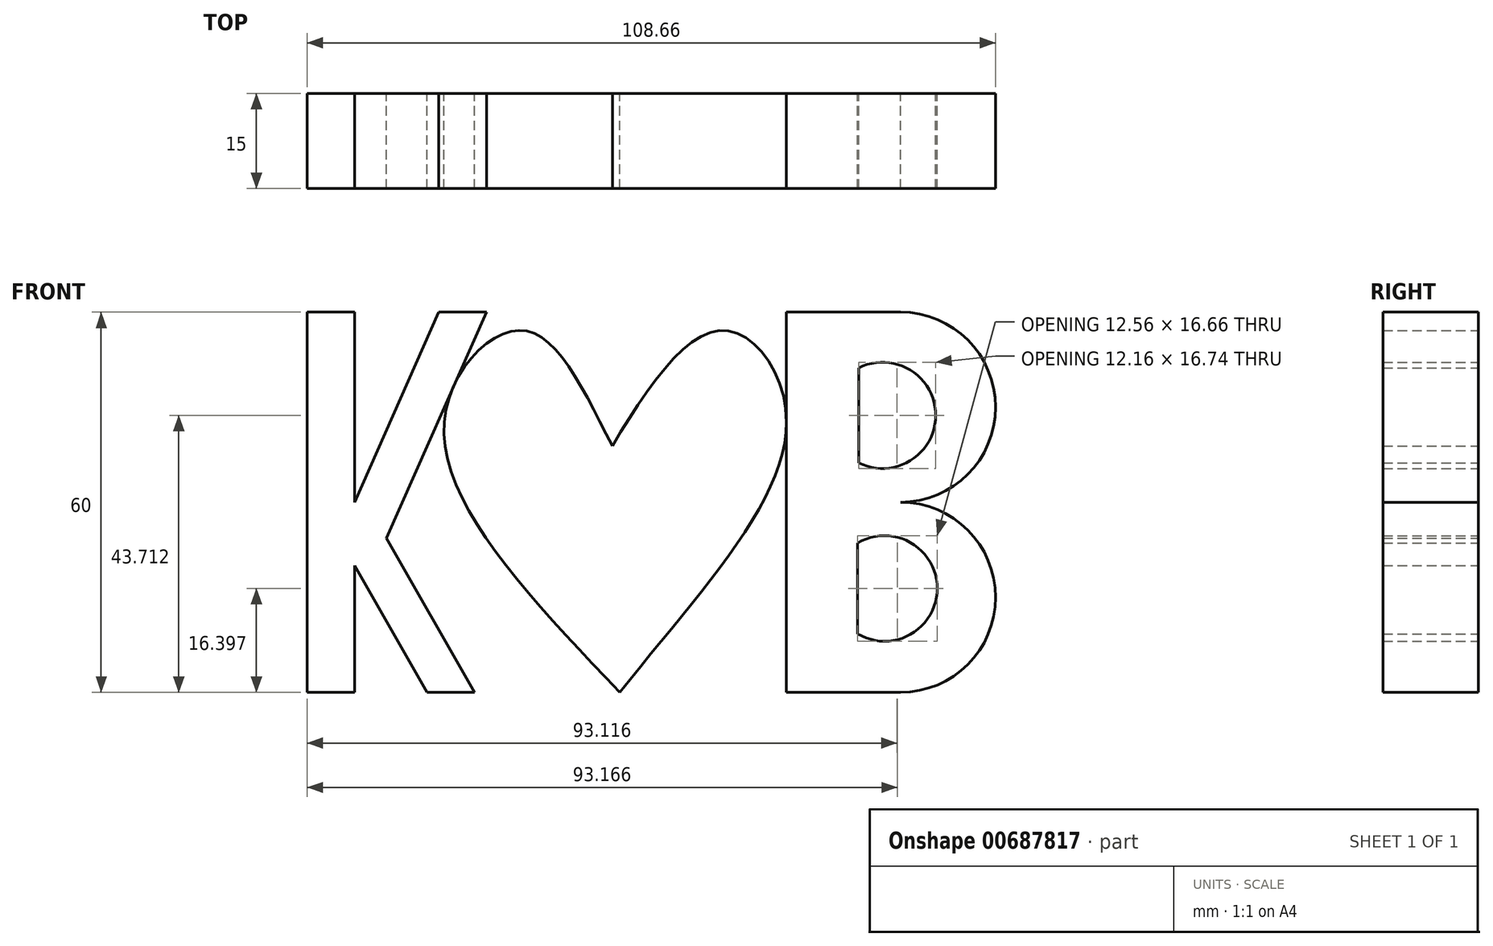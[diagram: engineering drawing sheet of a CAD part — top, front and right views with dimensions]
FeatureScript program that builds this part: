
annotation { "Feature Type Name" : "Feature", "Feature Type Description" : "" }
export const myFeature = defineFeature(function(context is Context, id is Id, definition is map)
    precondition{}
    {
        {
            var Q0;
            Q0=qCreatedBy(makeId("Front.planeOp"),FACE);
            var sketch = newSketch(context, id + "F0", { "sketchPlane" : qUnion([Q0])});
            skLineSegment(sketch, "E0", {"start": v(-21.67, 0) * mm, "end": v(-21.67, 30) * mm});
            skLineSegment(sketch, "E1", {"start": v(-21.67, 30) * mm, "end": v(-29.17, 30) * mm});
            skLineSegment(sketch, "E2", {"start": v(-29.17, 30) * mm, "end": v(-29.17, -30) * mm});
            skLineSegment(sketch, "E3", {"start": v(-29.17, -30) * mm, "end": v(-21.67, -30) * mm});
            skLineSegment(sketch, "E4", {"start": v(-21.67, -30) * mm, "end": v(-21.67, -10) * mm});
            skLineSegment(sketch, "E5", {"start": v(-21.67, -10) * mm, "end": v(-10.27, -30) * mm});
            skLineSegment(sketch, "E6", {"start": v(-10.27, -30) * mm, "end": v(-2.77, -30) * mm});
            skLineSegment(sketch, "E7", {"start": v(-21.67, 0) * mm, "end": v(-8.37, 30) * mm});
            skLineSegment(sketch, "E8", {"start": v(-8.37, 30) * mm, "end": v(-0.87, 30) * mm});
            skLineSegment(sketch, "E9", {"start": v(-2.77, -30) * mm, "end": v(-16.63, -5.67) * mm});
            skLineSegment(sketch, "E10", {"start": v(-16.63, -5.67) * mm, "end": v(-0.87, 30) * mm});
            skFitSpline(sketch, "E11", {"points": [v(20.16, -30) * mm, v(46.49, 12.65) * mm, v(36.71, 27.12) * mm, v(19, 8.86) * mm], "startDerivative": vector(86.6, 108.8) * mm, "endDerivative": vector(-53.17, -89.76) * mm});
            skFitSpline(sketch, "E12", {"points": [v(19, 8.86) * mm, v(4.64, 27.12) * mm, v(-7.53, 12.65) * mm, v(20.16, -30) * mm], "startDerivative": vector(-46.52, 90.14) * mm, "endDerivative": vector(98, -103.42) * mm});
            skLineSegment(sketch, "E13", {"start": v(46.49, 30) * mm, "end": v(46.49, -30) * mm});
            skPoint(sketch, "E13.startSnap0", {"position": v(-4.62, 30) * mm});
            skLineSegment(sketch, "E14", {"start": v(46.49, -30) * mm, "end": v(64.49, -30) * mm});
            skLineSegment(sketch, "E15", {"start": v(46.49, 30) * mm, "end": v(64.49, 30) * mm});
            skArc(sketch, "E16", {"start": v(64.49, 0) * mm, "mid": v(79.49, 15) * mm, "end": v(64.49, 30) * mm});
            skArc(sketch, "E17", {"start": v(64.49, -30) * mm, "mid": v(79.49, -15) * mm, "end": v(64.49, 0) * mm});
            skLineSegment(sketch, "E18", {"start": v(57.87, 21.19) * mm, "end": v(57.87, 6.23) * mm});
            skLineSegment(sketch, "E19", {"start": v(57.72, -6.43) * mm, "end": v(57.72, -20.78) * mm});
            skArc(sketch, "E20", {"start": v(57.87, 6.23) * mm, "mid": v(70.03, 13.71) * mm, "end": v(57.87, 21.19) * mm});
            skArc(sketch, "E21", {"start": v(57.72, -20.78) * mm, "mid": v(70.28, -13.6) * mm, "end": v(57.72, -6.43) * mm});
            skSolve(sketch);
        }
        {
            var Q0;
            Q0=makeQuery(id+"F0.imprint","IMPRINT",FACE,{"disambiguationData":[TD([[makeQuery(id+"F0.imprint","IMPRINT",EDGE,{"derivedFrom":sQuery(id+"F0.wireOp",EDGE,"E0")}),1.0]])]});
            var Q1;
            {var subQ0=sQuery(id+"F0.wireOp",EDGE,"E12");var subQ1=sQuery(id+"F0.wireOp",EDGE,"E11");var subQ2=makeQuery(id+"F0.imprint","INTERSECT",VERTEX,{"disambiguationData":[OD(0.0)],"derivedFrom":[subQ1,subQ0]});Q1=makeQuery(id+"F0.imprint","IMPRINT",FACE,{"disambiguationData":[TD([[makeQuery(id+"F0.imprint","IMPRINT",EDGE,{"disambiguationData":[TD([[subQ2,-1.0]])],"derivedFrom":subQ1}),1.0]])]});}
            var Q2;
            {var subQ5=sQuery(id+"F0.wireOp",EDGE,"E14");Q2=makeQuery(id+"F0.imprint","IMPRINT",FACE,{"disambiguationData":[TD([[makeQuery(id+"F0.imprint","IMPRINT",EDGE,{"derivedFrom":subQ5}),1.0]])]});}
            extrude(context, id + "F1", {"entities" : qUnion([Q0, Q1, Q2]), "depth" : 15 * mm, "offsetDistance" : 25 * mm});
        }
    });
